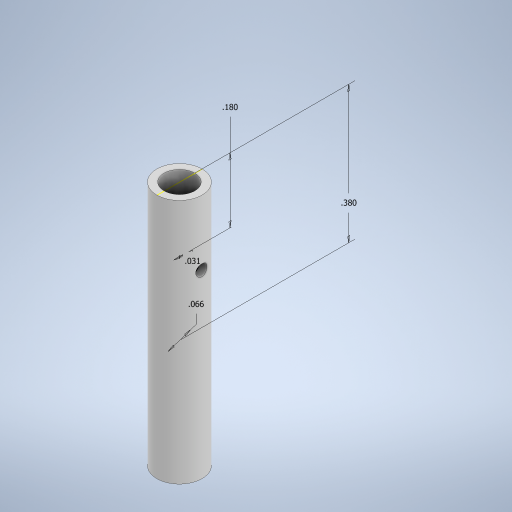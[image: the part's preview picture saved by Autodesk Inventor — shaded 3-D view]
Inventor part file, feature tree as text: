
AUTODESK INVENTOR PART (.ipt)
format: ipt  version: 2023 (Build 270158000, 158)  size: 256,512 bytes
history: native  units: in
note: dims shown in document units (in); Inventor stores cm internally (conversion verified against a paired STEP export)
features: extrude x3, sketch x2
ambient origin geometry x8: Origin, YZ Plane, XZ Plane, XY Plane, X Axis, Y Axis, Z Axis, Center Point
bodies: Solid1 (feature_tree)
feature tree (5):
  extrude  "Extrusion1"  Depth=0.125in
  sketch  "Sketch2"  dims[d2=0.68in d3=0.0in d4=0.066in d5=0.38in d6=0.68in d7=0.0in d8=0.0312in d9=0.18in d10=1.0in d11=0.0in]
  extrude  "Extrusion2"  Depth=0.066in
  extrude  "Extrusion3"  Depth=0.38in
  sketch  "Sketch1"  dims[d0=0.085in d1=0.125in]
